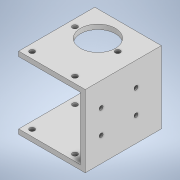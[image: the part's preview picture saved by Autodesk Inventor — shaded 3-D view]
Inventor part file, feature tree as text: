
AUTODESK INVENTOR PART (.ipt)
format: ipt  version: 2022 (Build 260153000, 153)  size: 168,960 bytes
history: native  units: mm
features: sketch x6, hole x4, extrude x2, other x1
ambient origin geometry x8: Origin, YZ Plane, XZ Plane, XY Plane, X Axis, Y Axis, Z Axis, Center Point
bodies: Body1 (feature_tree)
feature tree (13):
  other  "ソリッド1"
  extrude  "押し出し1"  Depth=48.0mm
  extrude  "押し出し2"  Depth=42.0mm
  hole  "穴1"  [1 undecoded]
  hole  "穴2"  [1 undecoded]
  hole  "穴3"  [1 undecoded]
  hole  "穴4"  [1 undecoded]
  sketch  "スケッチ1"
  sketch  "スケッチ2"
  sketch  "スケッチ3"
  sketch  "スケッチ4"
  sketch  "スケッチ5"
  sketch  "スケッチ6"
note: 4 required parameter values undecoded (feature->parameter linkage not recoverable at this tier; creation-order binding heuristic only, values carry confidence <= 0.55)
